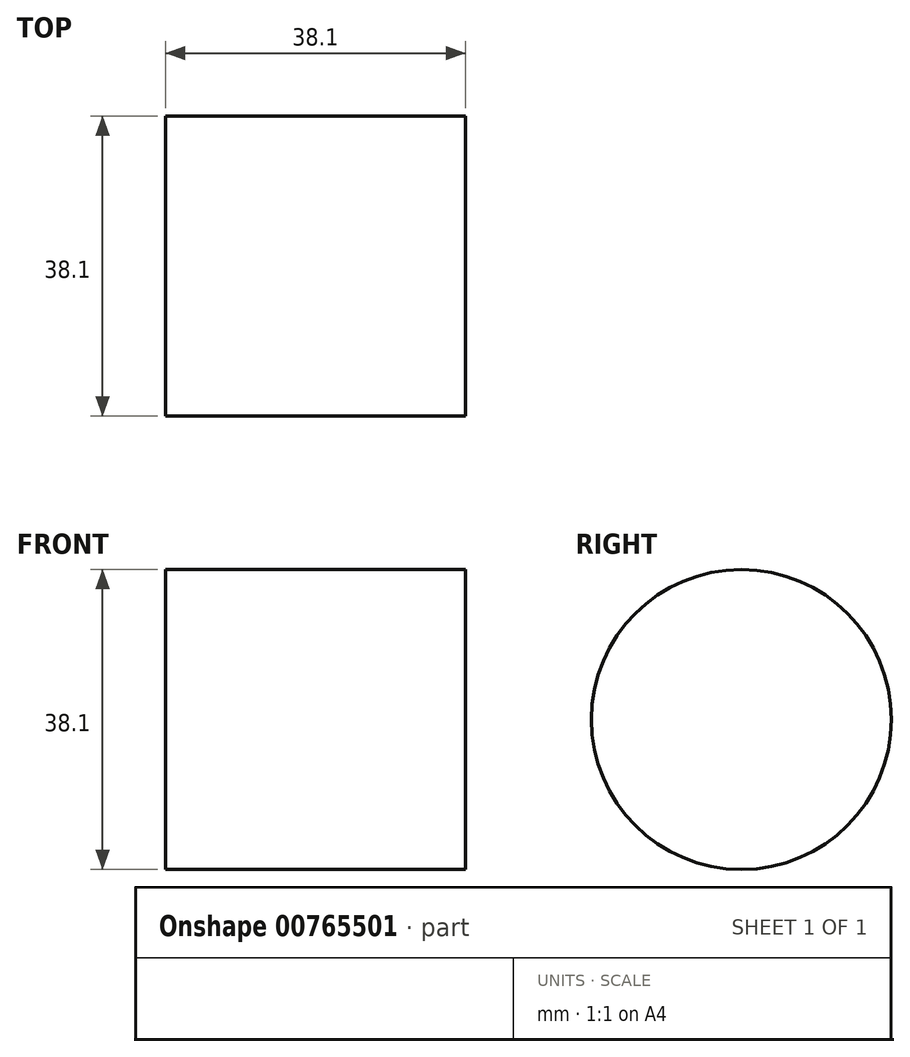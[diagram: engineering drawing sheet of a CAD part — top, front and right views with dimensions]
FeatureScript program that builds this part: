
annotation { "Feature Type Name" : "Feature", "Feature Type Description" : "" }
export const myFeature = defineFeature(function(context is Context, id is Id, definition is map)
    precondition{}
    {
        {
            var Q0;
            Q0=qCreatedBy(makeId("Right.planeOp"),FACE);
            var sketch = newSketch(context, id + "F0", { "sketchPlane" : qUnion([Q0])});
            skCircle(sketch, "E0", {"center": v(4.63, 0) * mm, "radius": 19.05 * mm});
            skSolve(sketch);
        }
        {
            var Q0;
            Q0 = qSketchRegion(id + "F0", true);
            extrude(context, id + "F1", {"entities" : qUnion([Q0]), "depth" : 38.1 * mm, "offsetDistance" : 25.4 * mm});
        }
    });
